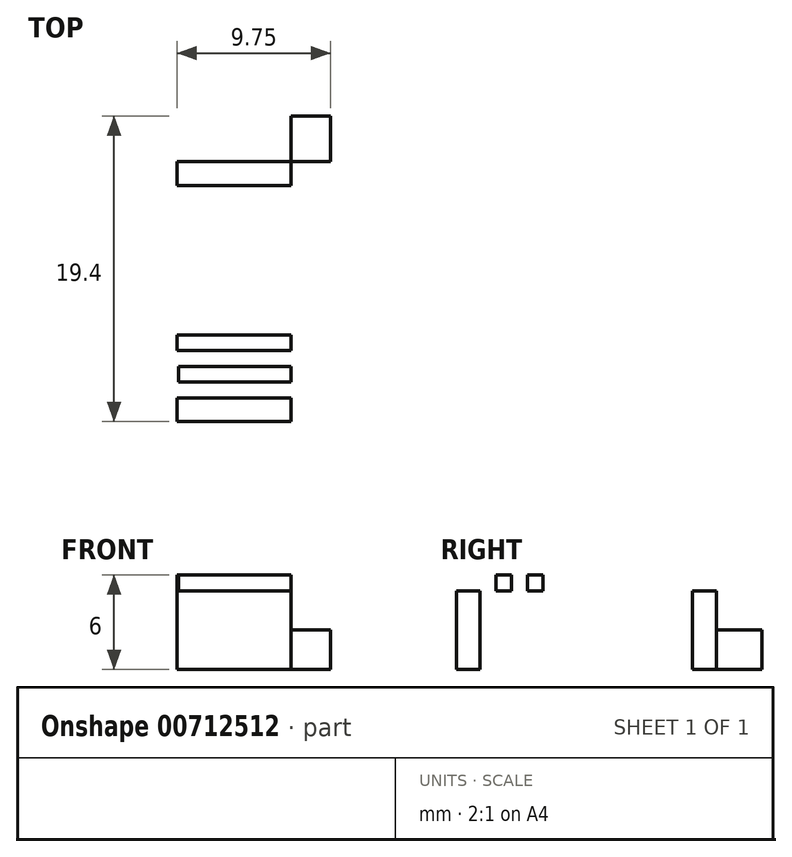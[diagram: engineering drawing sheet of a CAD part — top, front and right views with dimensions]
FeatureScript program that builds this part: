
annotation { "Feature Type Name" : "Feature", "Feature Type Description" : "" }
export const myFeature = defineFeature(function(context is Context, id is Id, definition is map)
    precondition{}
    {
        {
            var Q0;
            Q0=qCreatedBy(makeId("Top.planeOp"),FACE);
            var sketch = newSketch(context, id + "F0", { "sketchPlane" : qUnion([Q0])});
            skLineSegment(sketch, "E0.bottom", {"start": v(0, 0) * mm, "end": v(14.5, 0) * mm});
            skLineSegment(sketch, "E0.top", {"start": v(0, 7.5) * mm, "end": v(14.5, 7.5) * mm});
            skLineSegment(sketch, "E0.left", {"start": v(0, 0) * mm, "end": v(0, 7.5) * mm});
            skLineSegment(sketch, "E0.right", {"start": v(14.5, 0) * mm, "end": v(14.5, 7.5) * mm});
            skLineSegment(sketch, "E1.bottom", {"start": v(7.25, 0) * mm, "end": v(14.5, 0) * mm});
            skLineSegment(sketch, "E1.top", {"start": v(7.25, 1.5) * mm, "end": v(14.5, 1.5) * mm});
            skLineSegment(sketch, "E1.left", {"start": v(7.25, 0) * mm, "end": v(7.25, 1.5) * mm});
            skLineSegment(sketch, "E1.right", {"start": v(14.5, 0) * mm, "end": v(14.5, 1.5) * mm});
            skCircle(sketch, "E2", {"center": v(3.6, 3.75) * mm, "radius": 1.6 * mm});
            skSolve(sketch);
        }
        {
            var Q0;
            Q0=makeQuery(id+"F0.imprint","IMPRINT",FACE,{"disambiguationData":[TD([[makeQuery(id+"F0.imprint","IMPRINT",EDGE,{"derivedFrom":sQuery(id+"F0.wireOp",EDGE,"E0.bottom")}),1.0]])]});
            extrude(context, id + "F1", {"entities" : qUnion([Q0]), "depth" : 5 * mm, "offsetDistance" : 25 * mm});
        }
        {
            var Q0;
            Q0=makeQuery(id+"F1.opExtrude","SWEPT_FACE",FACE,{"disambiguationData":[OSD([sQuery(id+"F0.wireOp",EDGE,"E0.right")])]});
            var sketch = newSketch(context, id + "F2", { "sketchPlane" : qUnion([Q0])});
            skLineSegment(sketch, "E3.bottom", {"start": v(1.5, 0) * mm, "end": v(4.4, 0) * mm});
            skLineSegment(sketch, "E3.top", {"start": v(1.5, 2.5) * mm, "end": v(4.4, 2.5) * mm});
            skLineSegment(sketch, "E3.left", {"start": v(1.5, 0) * mm, "end": v(1.5, 2.5) * mm});
            skLineSegment(sketch, "E3.right", {"start": v(4.4, 0) * mm, "end": v(4.4, 2.5) * mm});
            skSolve(sketch);
        }
        {
            var Q0;
            Q0=makeQuery(id+"F2.imprint","IMPRINT",FACE,{"disambiguationData":[TD([[makeQuery(id+"F2.imprint","IMPRINT",EDGE,{"derivedFrom":sQuery(id+"F2.wireOp",EDGE,"E3.bottom")}),1.0]])]});
            extrude(context, id + "F3", {"entities" : qUnion([Q0]), "operationType" : NewBodyOperationType.ADD, "depth" : 2.5 * mm, "offsetDistance" : 25 * mm});
        }
        {
            var Q0;
            Q0=makeQuery(id+"F3.boolean.opBoolean","MERGE",FACE,{"derivedFrom":[makeQuery(id+"F1.opExtrude","CAP_FACE",FACE,{"disambiguationData":[OSD([sQuery(id+"F0.wireOp",EDGE,"E0.bottom"),sQuery(id+"F0.wireOp",EDGE,"E0.top"),sQuery(id+"F0.wireOp",EDGE,"E0.left"),sQuery(id+"F0.wireOp",EDGE,"E0.right"),sQuery(id+"F0.wireOp",EDGE,"E1.top"),sQuery(id+"F0.wireOp",EDGE,"E1.left"),sQuery(id+"F0.wireOp",EDGE,"E2")])],"isStart":true}),makeQuery(id+"F3.opExtrude","SWEPT_FACE",FACE,{"disambiguationData":[OSD([sQuery(id+"F2.wireOp",EDGE,"E3.bottom")])]})]});
            var sketch = newSketch(context, id + "F4", { "sketchPlane" : qUnion([Q0])});
            skCircle(sketch, "E4", {"center": v(3.6, -3.75) * mm, "radius": 3.1 * mm});
            skSolve(sketch);
        }
        {
            var Q0;
            Q0=makeQuery(id+"F4.imprint","IMPRINT",FACE,{"disambiguationData":[TD([[makeQuery(id+"F4.imprint","IMPRINT",EDGE,{"derivedFrom":sQuery(id+"F4.wireOp",EDGE,"E4")}),1.0]])]});
            extrude(context, id + "F5", {"entities" : qUnion([Q0]), "operationType" : NewBodyOperationType.REMOVE, "oppositeDirection" : true, "depth" : 2 * mm, "offsetDistance" : 25 * mm});
        }
        {
            var Q0;
            Q0=makeQuery(id+"F1.opExtrude","SWEPT_BODY",BODY,{"disambiguationData":[OSD([sQuery(id+"F0.wireOp",EDGE,"E0.bottom"),sQuery(id+"F0.wireOp",EDGE,"E0.top"),sQuery(id+"F0.wireOp",EDGE,"E0.left"),sQuery(id+"F0.wireOp",EDGE,"E0.right"),sQuery(id+"F0.wireOp",EDGE,"E1.top"),sQuery(id+"F0.wireOp",EDGE,"E1.left"),sQuery(id+"F0.wireOp",EDGE,"E2")])]});
            transform(context, id + "F6", {"entities" : qUnion([Q0]), "transformType" : TransformType.TRANSLATION_3D, "dx" : 0 * mm, "dy" : -15 * mm, "dz" : 0 * mm, "makeCopy" : true});
        }
        {
            var Q0;
            Q0=makeQuery(id+"F6.opPattern","COPY",FACE,{"derivedFrom":makeQuery(id+"F1.opExtrude","CAP_FACE",FACE,{"disambiguationData":[OSD([sQuery(id+"F0.wireOp",EDGE,"E0.bottom"),sQuery(id+"F0.wireOp",EDGE,"E0.top"),sQuery(id+"F0.wireOp",EDGE,"E0.left"),sQuery(id+"F0.wireOp",EDGE,"E0.right"),sQuery(id+"F0.wireOp",EDGE,"E1.top"),sQuery(id+"F0.wireOp",EDGE,"E1.left"),sQuery(id+"F0.wireOp",EDGE,"E2")])],"isStart":false}),"instanceName":"1"});
            var sketch = newSketch(context, id + "F7", { "sketchPlane" : qUnion([Q0])});
            skLineSegment(sketch, "E5.bottom", {"start": v(14.5, -13.5) * mm, "end": v(7.33, -13.5) * mm});
            skLineSegment(sketch, "E5.top", {"start": v(14.5, -12.5) * mm, "end": v(7.33, -12.5) * mm});
            skLineSegment(sketch, "E5.left", {"start": v(14.5, -13.5) * mm, "end": v(14.5, -12.5) * mm});
            skLineSegment(sketch, "E5.right", {"start": v(7.33, -13.5) * mm, "end": v(7.33, -12.5) * mm});
            skLineSegment(sketch, "E6.bottom", {"start": v(7.25, -10.5) * mm, "end": v(14.5, -10.5) * mm});
            skLineSegment(sketch, "E6.top", {"start": v(7.25, -9.5) * mm, "end": v(14.5, -9.5) * mm});
            skLineSegment(sketch, "E6.left", {"start": v(7.25, -10.5) * mm, "end": v(7.25, -9.5) * mm});
            skLineSegment(sketch, "E6.right", {"start": v(14.5, -10.5) * mm, "end": v(14.5, -9.5) * mm});
            skLineSegment(sketch, "E7.bottom", {"start": v(14.5, -7.5) * mm, "end": v(7.25, -7.5) * mm});
            skLineSegment(sketch, "E7.top", {"start": v(14.5, -8.5) * mm, "end": v(7.25, -8.5) * mm});
            skLineSegment(sketch, "E7.left", {"start": v(14.5, -7.5) * mm, "end": v(14.5, -8.5) * mm});
            skLineSegment(sketch, "E7.right", {"start": v(7.25, -7.5) * mm, "end": v(7.25, -8.5) * mm});
            skLineSegment(sketch, "E8.bottom", {"start": v(14.5, -11.5) * mm, "end": v(7.33, -11.5) * mm});
            skLineSegment(sketch, "E8.left", {"start": v(14.5, -11.5) * mm, "end": v(14.5, -12.5) * mm});
            skLineSegment(sketch, "E8.right", {"start": v(7.33, -11.5) * mm, "end": v(7.33, -12.5) * mm});
            skSolve(sketch);
        }
        {
            var Q0;
            Q0=makeQuery(id+"F7.imprint","IMPRINT",FACE,{"disambiguationData":[TD([[makeQuery(id+"F7.imprint","IMPRINT",EDGE,{"derivedFrom":sQuery(id+"F7.wireOp",EDGE,"E7.bottom")}),-1.0]])]});
            var Q1;
            Q1=makeQuery(id+"F7.imprint","IMPRINT",FACE,{"disambiguationData":[TD([[makeQuery(id+"F7.imprint","IMPRINT",EDGE,{"derivedFrom":sQuery(id+"F7.wireOp",EDGE,"E6.bottom")}),1.0]])]});
            var Q2;
            Q2=makeQuery(id+"F7.imprint","IMPRINT",FACE,{"disambiguationData":[TD([[makeQuery(id+"F7.imprint","IMPRINT",EDGE,{"derivedFrom":sQuery(id+"F7.wireOp",EDGE,"E8.bottom")}),1.0]])]});
            extrude(context, id + "F8", {"entities" : qUnion([Q0, Q1, Q2]), "operationType" : NewBodyOperationType.ADD, "depth" : 1 * mm, "offsetDistance" : 25 * mm});
        }
    });
